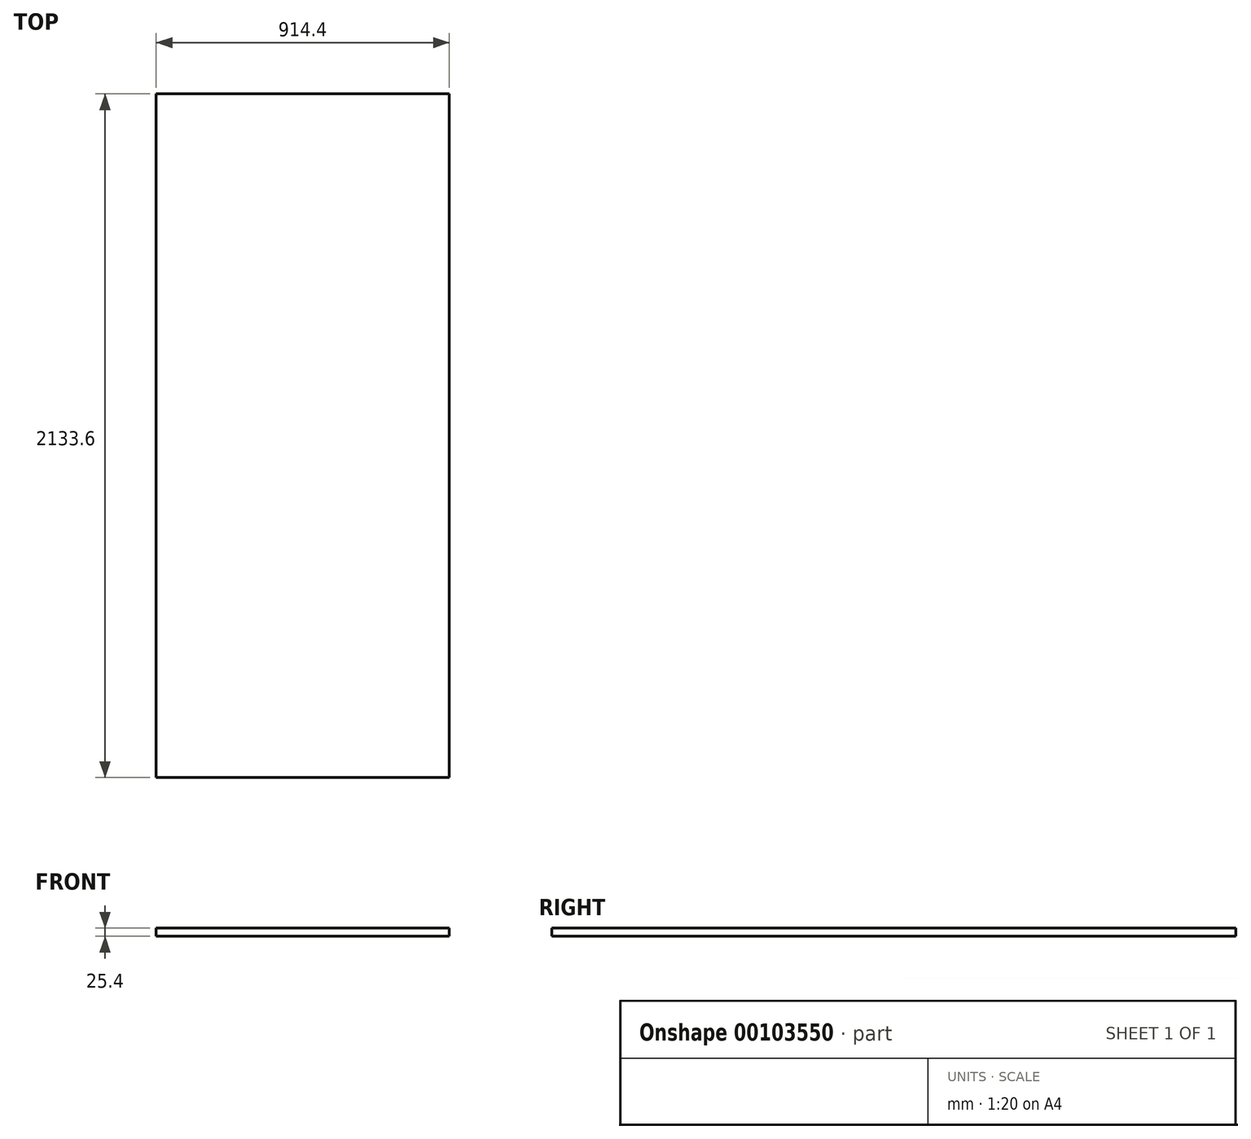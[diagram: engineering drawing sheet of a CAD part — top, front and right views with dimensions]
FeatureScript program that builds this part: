
annotation { "Feature Type Name" : "Feature", "Feature Type Description" : "" }
export const myFeature = defineFeature(function(context is Context, id is Id, definition is map)
    precondition{}
    {
        {
            var Q0;
            Q0=qCreatedBy(makeId("Top.planeOp"),FACE);
            var sketch = newSketch(context, id + "F0", { "sketchPlane" : qUnion([Q0])});
            skLineSegment(sketch, "E0.bottom", {"start": v(457.2, -1066.8) * mm, "end": v(-457.2, -1066.8) * mm});
            skLineSegment(sketch, "E0.top", {"start": v(457.2, 1066.8) * mm, "end": v(-457.2, 1066.8) * mm});
            skLineSegment(sketch, "E0.left", {"start": v(457.2, -1066.8) * mm, "end": v(457.2, 1066.8) * mm});
            skLineSegment(sketch, "E0.right", {"start": v(-457.2, -1066.8) * mm, "end": v(-457.2, 1066.8) * mm});
            skPoint(sketch, "E0.middle", {"position": v(0, 0) * mm});
            skLineSegment(sketch, "E1.bottom", {"start": v(304.8, -914.4) * mm, "end": v(-304.8, -914.4) * mm});
            skLineSegment(sketch, "E1.top", {"start": v(304.8, 914.4) * mm, "end": v(-304.8, 914.4) * mm});
            skLineSegment(sketch, "E1.left", {"start": v(304.8, -914.4) * mm, "end": v(304.8, 914.4) * mm});
            skLineSegment(sketch, "E1.right", {"start": v(-304.8, -914.4) * mm, "end": v(-304.8, 914.4) * mm});
            skSolve(sketch);
        }
        {
            var Q0;
            Q0=makeQuery(id+"F0.imprint","IMPRINT",FACE,{"disambiguationData":[TD([[makeQuery(id+"F0.imprint","IMPRINT",EDGE,{"derivedFrom":sQuery(id+"F0.wireOp",EDGE,"E0.bottom")}),-1.0]])]});
            var Q1;
            Q1=makeQuery(id+"F0.imprint","IMPRINT",FACE,{"disambiguationData":[TD([[makeQuery(id+"F0.imprint","IMPRINT",EDGE,{"derivedFrom":sQuery(id+"F0.wireOp",EDGE,"E1.bottom")}),-1.0]])]});
            extrude(context, id + "F1", {"entities" : qUnion([Q0, Q1]), "depth" : 25.4 * mm});
        }
    });
